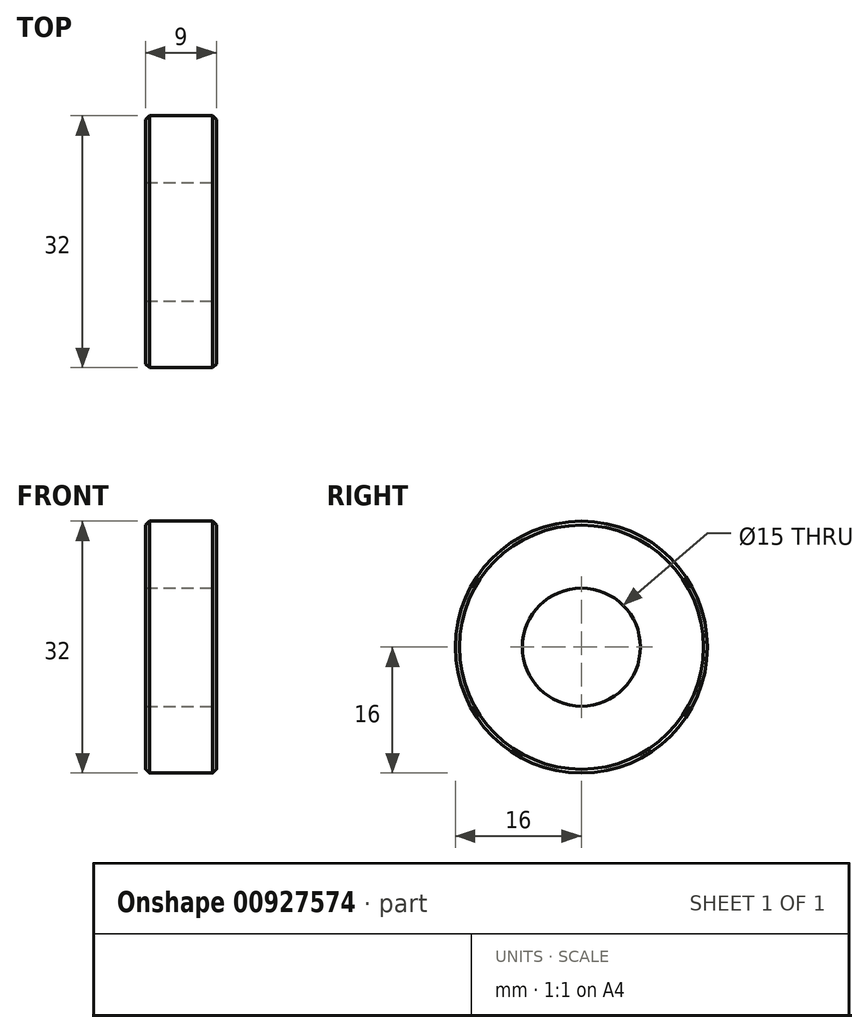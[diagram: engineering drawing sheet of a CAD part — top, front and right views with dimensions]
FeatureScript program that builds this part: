
annotation { "Feature Type Name" : "Feature", "Feature Type Description" : "" }
export const myFeature = defineFeature(function(context is Context, id is Id, definition is map)
    precondition{}
    {
        {
            var Q0;
            Q0=qCreatedBy(makeId("Right.planeOp"),FACE);
            var sketch = newSketch(context, id + "F0", { "sketchPlane" : qUnion([Q0])});
            skCircle(sketch, "E0", {"center": v(0, 0) * mm, "radius": 16 * mm});
            skSolve(sketch);
        }
        {
            var Q0;
            Q0 = qSketchRegion(id + "F0", true);
            extrude(context, id + "F1", {"entities" : qUnion([Q0]), "oppositeDirection" : true, "depth" : 9 * mm, "offsetDistance" : 25 * mm});
        }
        {
            var Q0;
            Q0=makeQuery(id+"F1.opExtrude","CAP_FACE",FACE,{"disambiguationData":[OSD([sQuery(id+"F0.wireOp",EDGE,"E0")])],"isStart":true});
            var sketch = newSketch(context, id + "F2", { "sketchPlane" : qUnion([Q0])});
            skCircle(sketch, "E1", {"center": v(0, 0) * mm, "radius": 7.5 * mm});
            skSolve(sketch);
        }
        {
            var Q0;
            Q0=makeQuery(id+"F2.imprint","IMPRINT",FACE,{"disambiguationData":[TD([[makeQuery(id+"F2.imprint","IMPRINT",EDGE,{"derivedFrom":sQuery(id+"F2.wireOp",EDGE,"E1")}),1.0]])]});
            extrude(context, id + "F3", {"entities" : qUnion([Q0]), "operationType" : NewBodyOperationType.REMOVE, "endBound" : BoundingType.THROUGH_ALL, "oppositeDirection" : true, "depth" : 25 * mm, "offsetDistance" : 25 * mm});
        }
        {
            var Q0;
            Q0=makeQuery(id+"F1.opExtrude","SWEPT_FACE",FACE,{"disambiguationData":[OSD([sQuery(id+"F0.wireOp",EDGE,"E0")])]});
            chamfer(context, id + "F4", {"entities" : qUnion([Q0]), "width" : 0.5 * mm, "tangentPropagation" : true});
        }
    });
